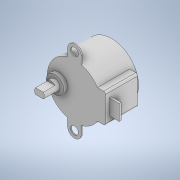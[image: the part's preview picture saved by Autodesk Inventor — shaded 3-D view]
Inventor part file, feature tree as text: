
AUTODESK INVENTOR PART (.ipt)
format: ipt  version: 2021 (Build 250183000, 183)  size: 199,168 bytes
history: native  units: mm
features: sketch x8, extrude x7, fillet x2, hole x1
ambient origin geometry x8: Origin, YZ Plane, XZ Plane, XY Plane, X Axis, Y Axis, Z Axis, Center Point
bodies: Solid1 (feature_tree)
feature tree (18):
  extrude  "Extrusion1"  Depth=19.0mm TaperAngle=0.0deg
  extrude  "Extrusion2"  Depth=10.0mm
  fillet  "Fillet1"  Radius=16.0mm
  extrude  "Extrusion3"  Depth=16.5mm TaperAngle=0.0deg
  extrude  "Extrusion4"  Depth=9.0mm
  extrude  "Extrusion5"  Depth=8.0mm
  extrude  "Extrusion6"  Depth=5.0mm
  extrude  "Extrusion7"  Depth=3.0mm
  fillet  "Fillet2"  Radius=1.5mm
  hole  "Hole1"  [1 undecoded]
  sketch  "Sketch1"  dims[d0=28.0mm d1=19.0mm d2=0.0mm]
  sketch  "Sketch2"  dims[d3=15.0mm d4=10.0mm d5=16.0mm]
  sketch  "Sketch3"  dims[d6=7.5mm d7=16.5mm d8=0.0mm]
  sketch  "Sketch4"  dims[d9=1.0mm d10=9.0mm]
  sketch  "Sketch5"  dims[d11=0.0mm d12=8.0mm]
  sketch  "Sketch6"  dims[d13=2.0mm d14=0.0mm d15=5.0mm]
  sketch  "Sketch7"  dims[d16=8.0mm d17=0.0mm d18=3.0mm d19=1.5mm]
  sketch  "Sketch8"  dims[d20=6.0mm d21=0.0mm d22=2.0mm d23=1.0mm d24=3.5mm d25=3.5mm d26=5.0mm d27=0.0mm d28=7.0mm d29=7.0mm d30=3.5mm d31=2.0mm d32=7.0mm d33=7.0mm d34=2.0mm d35=3.5mm d36=0.5mm d37=0.0mm d38=3.5mm d39=0.0mm d40=4.0mm d41=6.0mm d42=4.0mm d43=2.0mm d44=90.0deg d45=1.0mm d46=20.594885mm]
note: 1 required parameter value undecoded (feature->parameter linkage not recoverable at this tier; creation-order binding heuristic only, values carry confidence <= 0.55)
